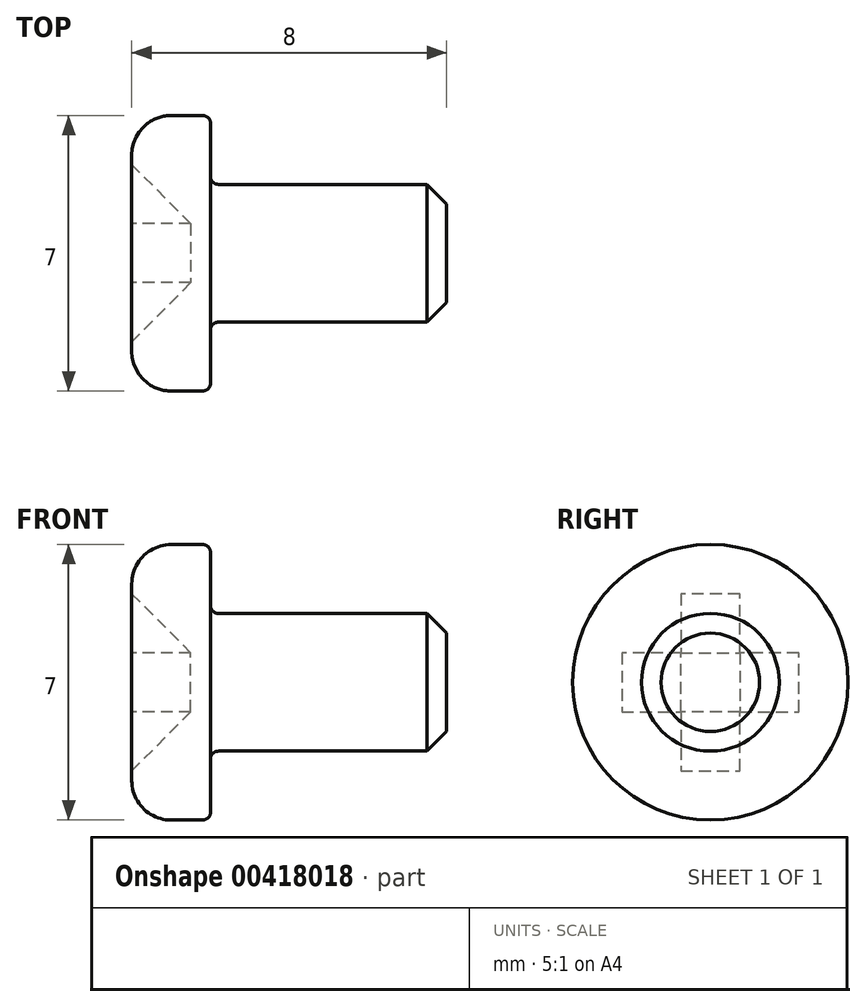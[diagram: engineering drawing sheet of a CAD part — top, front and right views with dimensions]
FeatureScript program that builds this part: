
annotation { "Feature Type Name" : "Feature", "Feature Type Description" : "" }
export const myFeature = defineFeature(function(context is Context, id is Id, definition is map)
    precondition{}
    {
        {
            var Q0;
            Q0=qCreatedBy(makeId("Top.planeOp"),FACE);
            var sketch = newSketch(context, id + "F0", { "sketchPlane" : qUnion([Q0])});
            skLineSegment(sketch, "E0", {"start": v(0, 0) * mm, "end": v(0, 3.5) * mm});
            skLineSegment(sketch, "E1", {"start": v(0, 3.5) * mm, "end": v(2, 3.5) * mm});
            skLineSegment(sketch, "E2", {"start": v(2, 3.5) * mm, "end": v(2, 1.75) * mm});
            skLineSegment(sketch, "E3", {"start": v(2, 1.75) * mm, "end": v(8, 1.75) * mm});
            skLineSegment(sketch, "E4", {"start": v(8, 1.75) * mm, "end": v(8, 0) * mm});
            skLineSegment(sketch, "E5", {"start": v(8, 0) * mm, "end": v(0, 0) * mm});
            skSolve(sketch);
        }
        {
            var Q0;
            Q0=makeQuery(id+"F0.imprint","IMPRINT",FACE,{"disambiguationData":[TD([[makeQuery(id+"F0.imprint","IMPRINT",EDGE,{"derivedFrom":sQuery(id+"F0.wireOp",EDGE,"E0")}),-1.0]])]});
            var Q1;
            Q1=sQuery(id+"F0.wireOp",EDGE,"E5");
            revolve(context, id + "F1", {"entities" : qUnion([Q0]), "axis" : qUnion([Q1]), "revolveType" : RevolveType.FULL});
        }
        {
            var Q0;
            Q0=makeQuery(id+"F1.opRevolve","SWEPT_EDGE",EDGE,{"disambiguationData":[OSD([sQuery(id+"F0.wireOp",EDGE,"E3"),sQuery(id+"F0.wireOp",EDGE,"E4")])]});
            chamfer(context, id + "F2", {"entities" : qUnion([Q0]), "width" : 0.5 * mm, "tangentPropagation" : true});
        }
        {
            var Q0;
            Q0=makeQuery(id+"F1.opRevolve","SWEPT_EDGE",EDGE,{"disambiguationData":[OSD([sQuery(id+"F0.wireOp",EDGE,"E2"),sQuery(id+"F0.wireOp",EDGE,"E3")])]});
            fillet(context, id + "F3", {"entities" : qUnion([Q0]), "radius" : 0.2 * mm, "tangentPropagation" : true, "allowEdgeOverflow" : false});
        }
        {
            var Q0;
            Q0=makeQuery(id+"F1.opRevolve","SWEPT_EDGE",EDGE,{"disambiguationData":[OSD([sQuery(id+"F0.wireOp",EDGE,"E1"),sQuery(id+"F0.wireOp",EDGE,"E2")])]});
            fillet(context, id + "F4", {"entities" : qUnion([Q0]), "radius" : 0.2 * mm, "tangentPropagation" : true, "allowEdgeOverflow" : false});
        }
        {
            var Q0;
            Q0=makeQuery(id+"F1.opRevolve","SWEPT_EDGE",EDGE,{"disambiguationData":[OSD([sQuery(id+"F0.wireOp",EDGE,"E0"),sQuery(id+"F0.wireOp",EDGE,"E1")])]});
            fillet(context, id + "F5", {"entities" : qUnion([Q0]), "radius" : 1 * mm, "tangentPropagation" : true, "allowEdgeOverflow" : false});
        }
        {
            var Q0;
            Q0=makeQuery(id+"F1.opRevolve","SWEPT_FACE",FACE,{"disambiguationData":[OSD([sQuery(id+"F0.wireOp",EDGE,"E0")])]});
            var sketch = newSketch(context, id + "F6", { "sketchPlane" : qUnion([Q0])});
            skLineSegment(sketch, "E6", {"start": v(-0.75, 0.75) * mm, "end": v(-0.75, 2.25) * mm});
            skLineSegment(sketch, "E7", {"start": v(-0.75, 2.25) * mm, "end": v(0.75, 2.25) * mm});
            skLineSegment(sketch, "E8", {"start": v(0.75, 2.25) * mm, "end": v(0.75, 0.75) * mm});
            skLineSegment(sketch, "E9", {"start": v(0.75, 0.75) * mm, "end": v(2.25, 0.75) * mm});
            skLineSegment(sketch, "E10", {"start": v(2.25, 0.75) * mm, "end": v(2.25, -0.75) * mm});
            skLineSegment(sketch, "E11", {"start": v(2.25, -0.75) * mm, "end": v(0.75, -0.75) * mm});
            skLineSegment(sketch, "E12", {"start": v(0.75, -0.75) * mm, "end": v(0.75, -2.25) * mm});
            skLineSegment(sketch, "E13", {"start": v(0.75, -2.25) * mm, "end": v(-0.75, -2.25) * mm});
            skLineSegment(sketch, "E14", {"start": v(-0.75, -2.25) * mm, "end": v(-0.75, -0.75) * mm});
            skLineSegment(sketch, "E15", {"start": v(-0.75, -0.75) * mm, "end": v(-2.25, -0.75) * mm});
            skLineSegment(sketch, "E16", {"start": v(-2.25, -0.75) * mm, "end": v(-2.25, 0.75) * mm});
            skLineSegment(sketch, "E17", {"start": v(-2.25, 0.75) * mm, "end": v(-0.75, 0.75) * mm});
            skLineSegment(sketch, "E18", {"start": v(-0.75, 0.75) * mm, "end": v(0.75, -0.75) * mm, "construction": true});
            skLineSegment(sketch, "E19", {"start": v(0.75, 0.75) * mm, "end": v(-0.75, -0.75) * mm, "construction": true});
            skPoint(sketch, "E20", {"position": v(0, 0) * mm});
            skSolve(sketch);
        }
        {
            var Q0;
            Q0=makeQuery(id+"F6.imprint","IMPRINT",FACE,{"disambiguationData":[TD([[makeQuery(id+"F6.imprint","IMPRINT",EDGE,{"derivedFrom":sQuery(id+"F6.wireOp",EDGE,"E6")}),-1.0]])]});
            extrude(context, id + "F7", {"entities" : qUnion([Q0]), "operationType" : NewBodyOperationType.REMOVE, "oppositeDirection" : true, "depth" : 1.5 * mm});
        }
        {
            var Q0;
            Q0=makeQuery(id+"F7.boolean.opBoolean","COPY",EDGE,{"derivedFrom":makeQuery(id+"F7.opExtrude","CAP_EDGE",EDGE,{"disambiguationData":[OSD([sQuery(id+"F6.wireOp",EDGE,"E16")])],"isStart":false})});
            var Q1;
            Q1=makeQuery(id+"F7.boolean.opBoolean","COPY",EDGE,{"derivedFrom":makeQuery(id+"F7.opExtrude","CAP_EDGE",EDGE,{"disambiguationData":[OSD([sQuery(id+"F6.wireOp",EDGE,"E7")])],"isStart":false})});
            var Q2;
            Q2=makeQuery(id+"F7.boolean.opBoolean","COPY",EDGE,{"derivedFrom":makeQuery(id+"F7.opExtrude","CAP_EDGE",EDGE,{"disambiguationData":[OSD([sQuery(id+"F6.wireOp",EDGE,"E13")])],"isStart":false})});
            var Q3;
            Q3=makeQuery(id+"F7.boolean.opBoolean","COPY",EDGE,{"derivedFrom":makeQuery(id+"F7.opExtrude","CAP_EDGE",EDGE,{"disambiguationData":[OSD([sQuery(id+"F6.wireOp",EDGE,"E10")])],"isStart":false})});
            chamfer(context, id + "F8", {"entities" : qUnion([Q0, Q1, Q2, Q3]), "width" : 1.5 * mm, "tangentPropagation" : true});
        }
    });
